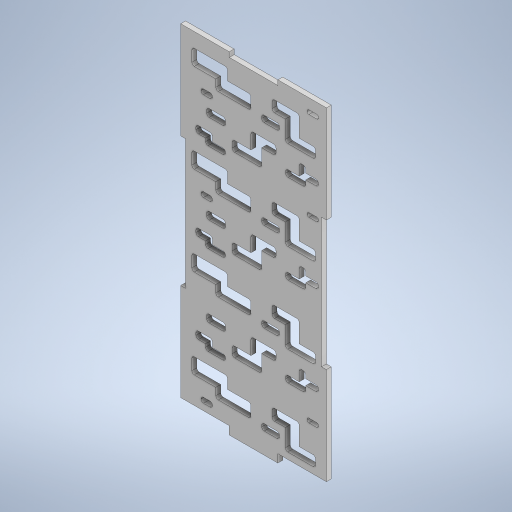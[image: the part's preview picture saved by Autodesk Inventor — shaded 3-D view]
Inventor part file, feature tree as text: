
AUTODESK INVENTOR PART (.ipt)
format: ipt  version: 2023 (Build 270158000, 158)  size: 775,168 bytes
history: native  units: mm
features: extrude x2, sketch x1
ambient origin geometry x8: Origin, YZ Plane, XZ Plane, XY Plane, X Axis, Y Axis, Z Axis, Center Point
bodies: Solide1 (feature_tree)
feature tree (3):
  extrude  "Extrusion1"  Depth=90.0mm
  extrude  "Extrusion2"  Depth=200.0mm
  sketch  "Esquisse1"
